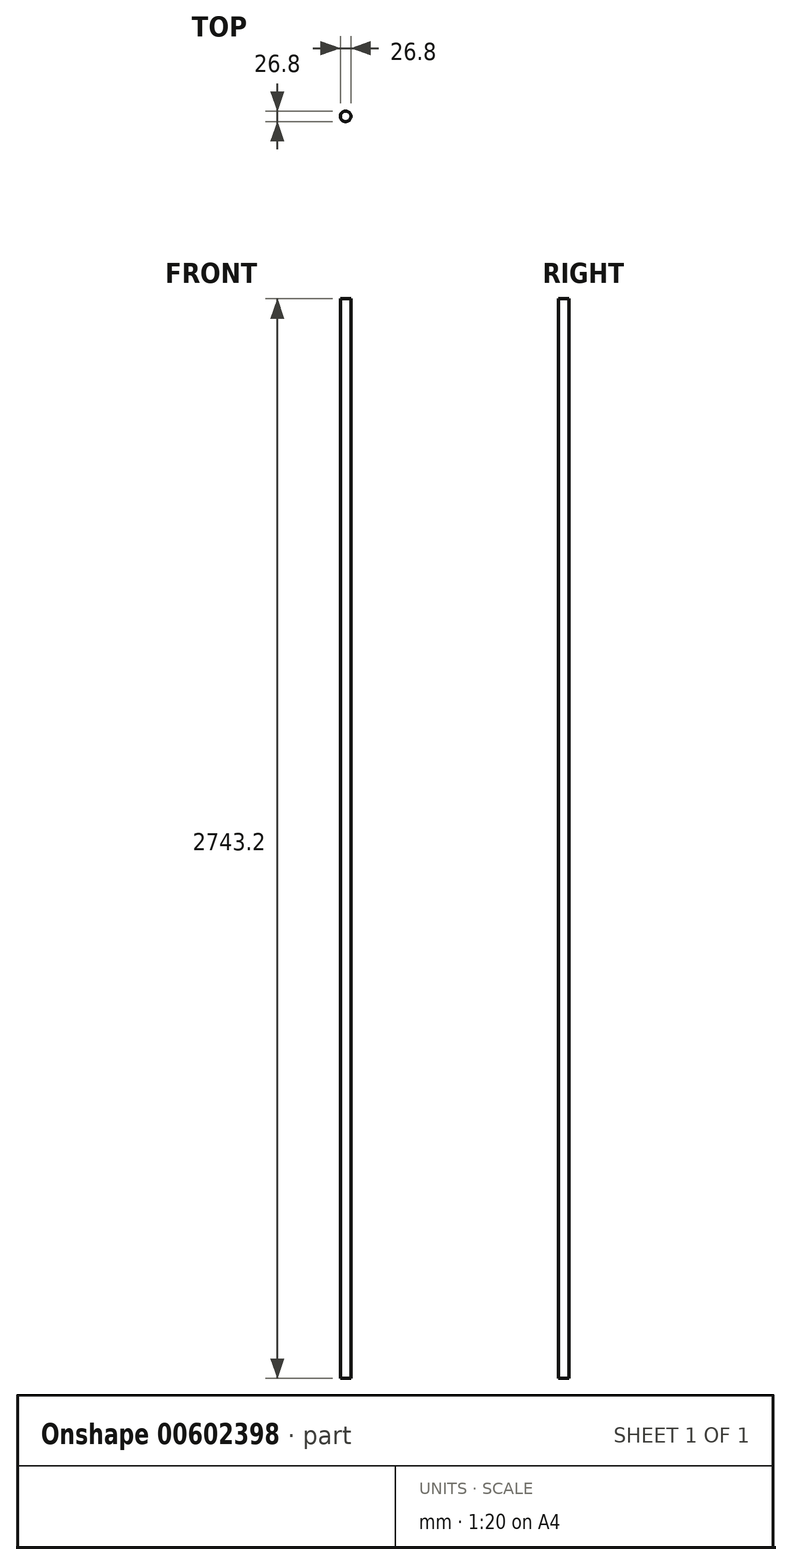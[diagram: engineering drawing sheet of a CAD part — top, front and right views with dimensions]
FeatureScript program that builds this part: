
annotation { "Feature Type Name" : "Feature", "Feature Type Description" : "" }
export const myFeature = defineFeature(function(context is Context, id is Id, definition is map)
    precondition{}
    {
        {
            var Q0;
            Q0=qCreatedBy(makeId("Top.planeOp"),FACE);
            var sketch = newSketch(context, id + "F0", { "sketchPlane" : qUnion([Q0])});
            skCircle(sketch, "E0", {"center": v(0, 0) * mm, "radius": 13.4 * mm});
            skSolve(sketch);
        }
        {
            var Q0;
            Q0=makeQuery(id+"F0.imprint","IMPRINT",FACE,{"disambiguationData":[TD([[makeQuery(id+"F0.imprint","IMPRINT",EDGE,{"derivedFrom":sQuery(id+"F0.wireOp",EDGE,"E0")}),1.0]])]});
            extrude(context, id + "F1", {"entities" : qUnion([Q0]), "depth" : 2743.2 * mm, "offsetDistance" : 30.48 * mm});
        }
    });
